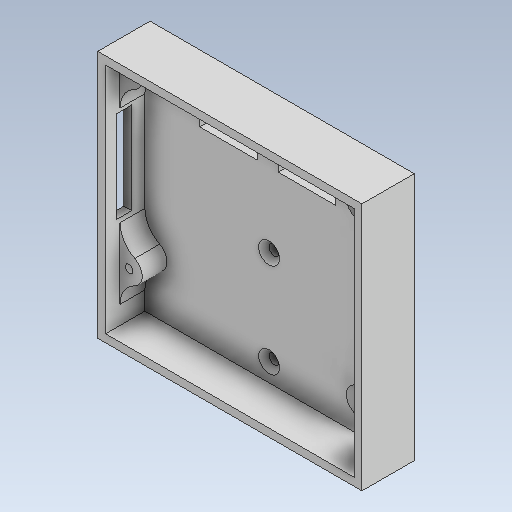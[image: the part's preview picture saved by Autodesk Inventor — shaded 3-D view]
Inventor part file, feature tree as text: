
AUTODESK INVENTOR PART (.ipt)
format: ipt  version: 2020 (Build 240168000, 168)  size: 210,432 bytes
history: native  units: mm
features: reference x14, sketch x6, extrude x5, other x5, fillet x1, hole x1, projected_geometry x1
ambient origin geometry x8: Origin, YZ Plane, XZ Plane, XY Plane, X Axis, Y Axis, Z Axis, Center Point
bodies: Solid1 (feature_tree)
feature tree (33):
  extrude  "Extrusion1"  Depth=101.0mm
  extrude  "Extrusion2"  Depth=3.0mm
  extrude  "Extrusion3"  Depth=15.0mm
  extrude  "Extrusion4"  TaperAngle=0.0deg  [1 undecoded]
  fillet  "Fillet1"  Radius=10.0mm
  extrude  "Extrusion5"  Depth=10.0mm
  hole  "Hole2"  [1 undecoded]
  sketch  "Sketch1"  dims[d0=95.0mm d1=101.0mm]
  sketch  "Sketch2"  dims[d2=20.0mm d3=0.0mm d4=3.0mm]
  projected_geometry  "Projected Loop1"
  sketch  "Sketch3"  dims[d5=15.0mm d6=0.0mm d7=1.0mm]
  reference  "Reference1"
  reference  "Reference2"
  reference  "Reference3"
  reference  "Reference4"
  reference  "Reference5"
  reference  "Reference6"
  reference  "Reference7"
  reference  "Reference8"
  sketch  "Sketch4"  dims[d8=1.0mm d9=0.0mm d10=0.0mm d11=10.0mm]
  reference  "Reference9"
  reference  "Reference10"
  reference  "Reference11"
  reference  "Reference12"
  sketch  "Sketch7"  dims[d12=10.0mm d13=10.0mm]
  sketch  "Sketch9"  dims[d14=10.0mm d15=9.5mm d16=0.0mm d17=10.0mm d18=6.0mm d19=35.0mm d20=4.0mm d21=38.75mm d22=9.5mm d23=0.0mm d31=4.0mm d32=6.0mm d33=8.0mm d34=2.0mm d35=90.0deg d36=8.0mm d37=20.594885mm]
  reference  "Reference19"
  reference  "Reference20"
  parser-record x1  (decoder bookkeeping rows leaked as tree rows — omitted from the tree; the rows remain in map.json)
  other  "10-06-01 ansamblu display.iam"
  other  "10-06-03 ReprapDiscountFullGraphicSmartController-Robotale_Dummy:1"
  other  "<path> 3D Ansamblu_General.iam"
  other  "I.A.B 3D Ansamblu_General.iam"
note: 2 required parameter values undecoded (feature->parameter linkage not recoverable at this tier; creation-order binding heuristic only, values carry confidence <= 0.55)
note: 2 file-system paths scrubbed to <path> (originals preserved in map.json)
